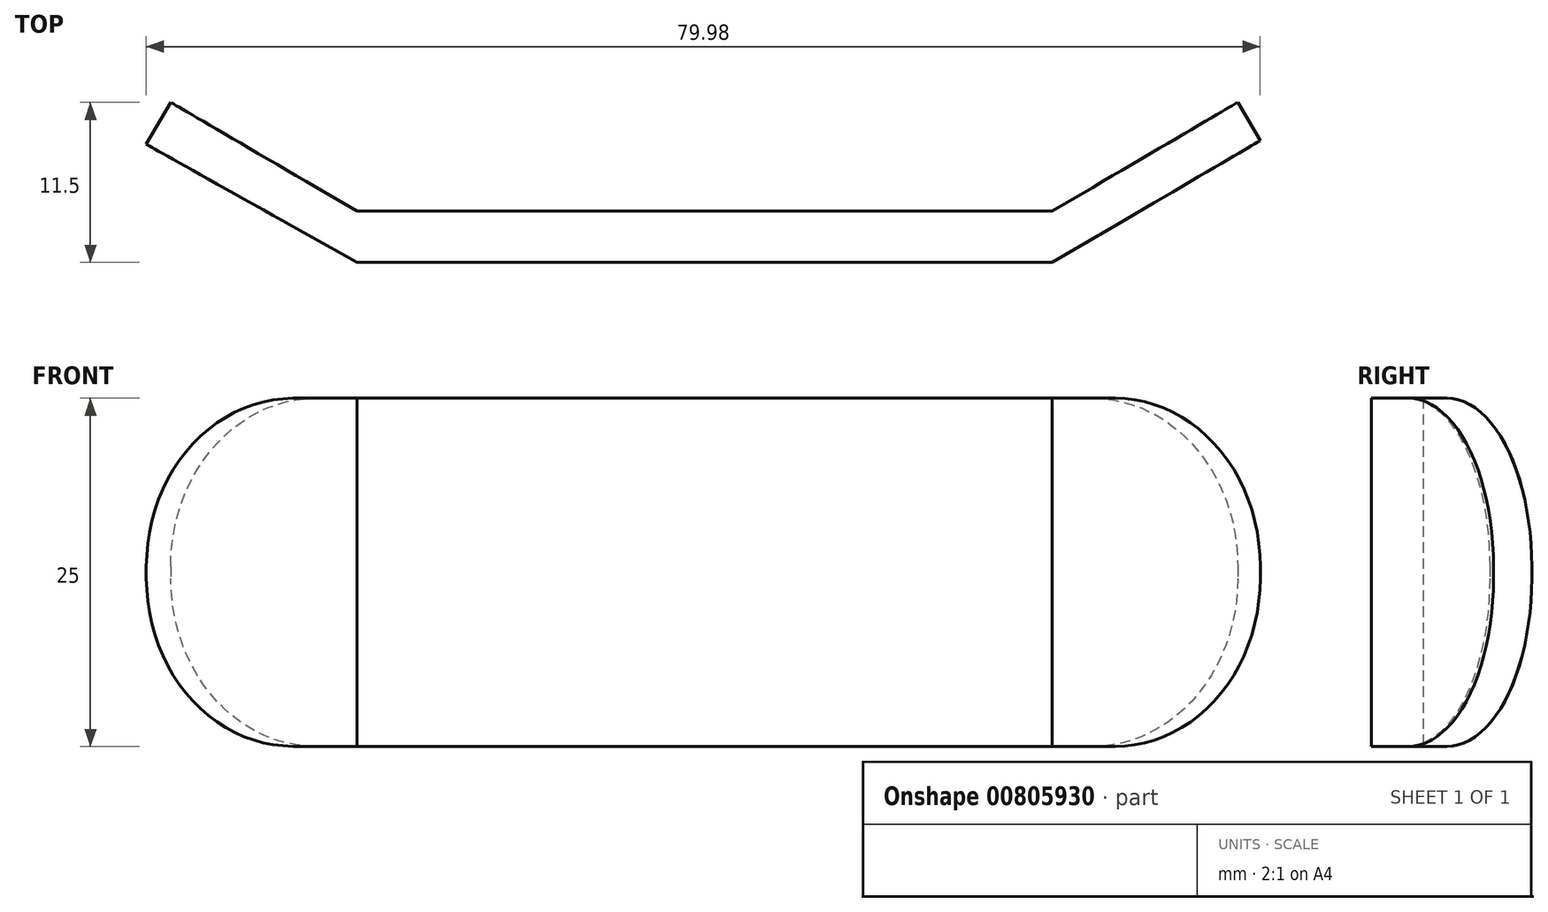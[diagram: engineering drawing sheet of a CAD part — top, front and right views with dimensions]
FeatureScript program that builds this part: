
annotation { "Feature Type Name" : "Feature", "Feature Type Description" : "" }
export const myFeature = defineFeature(function(context is Context, id is Id, definition is map)
    precondition{}
    {
        {
            var Q0;
            Q0=qCreatedBy(makeId("Top.planeOp"),FACE);
            var sketch = newSketch(context, id + "F0", { "sketchPlane" : qUnion([Q0])});
            skLineSegment(sketch, "E0", {"start": v(-60.16, 15.32) * mm, "end": v(-58.4, 18.34) * mm});
            skLineSegment(sketch, "E1", {"start": v(-58.4, 18.34) * mm, "end": v(-45.02, 10.53) * mm});
            skLineSegment(sketch, "E2", {"start": v(-45.02, 10.53) * mm, "end": v(4.9, 10.53) * mm});
            skLineSegment(sketch, "E3", {"start": v(4.9, 10.53) * mm, "end": v(18.21, 18.34) * mm});
            skLineSegment(sketch, "E4", {"start": v(18.21, 18.34) * mm, "end": v(19.82, 15.6) * mm});
            skLineSegment(sketch, "E5", {"start": v(19.82, 15.6) * mm, "end": v(4.9, 6.84) * mm});
            skLineSegment(sketch, "E6", {"start": v(4.9, 6.84) * mm, "end": v(-45.02, 6.84) * mm});
            skLineSegment(sketch, "E7", {"start": v(-45.02, 6.84) * mm, "end": v(-60.16, 15.32) * mm});
            skSolve(sketch);
        }
        {
            var Q0;
            Q0 = qSketchRegion(id + "F0", true);
            extrude(context, id + "F1", {"entities" : qUnion([Q0]), "depth" : 25 * mm, "offsetDistance" : 25 * mm});
        }
        {
            var Q0;
            Q0=makeQuery(id+"F1.opExtrude","CAP_EDGE",EDGE,{"disambiguationData":[OSD([sQuery(id+"F0.wireOp",EDGE,"E0")])],"isStart":false});
            var Q1;
            Q1=makeQuery(id+"F1.opExtrude","CAP_EDGE",EDGE,{"disambiguationData":[OSD([sQuery(id+"F0.wireOp",EDGE,"E0")])],"isStart":true});
            var Q2;
            Q2=makeQuery(id+"F1.opExtrude","CAP_EDGE",EDGE,{"disambiguationData":[OSD([sQuery(id+"F0.wireOp",EDGE,"E4")])],"isStart":false});
            var Q3;
            Q3=makeQuery(id+"F1.opExtrude","CAP_EDGE",EDGE,{"disambiguationData":[OSD([sQuery(id+"F0.wireOp",EDGE,"E4")])],"isStart":true});
            fillet(context, id + "F2", {"entities" : qUnion([Q0, Q1, Q2, Q3]), "radius" : 12.07 * mm, "tangentPropagation" : true, "allowEdgeOverflow" : false});
        }
    });
